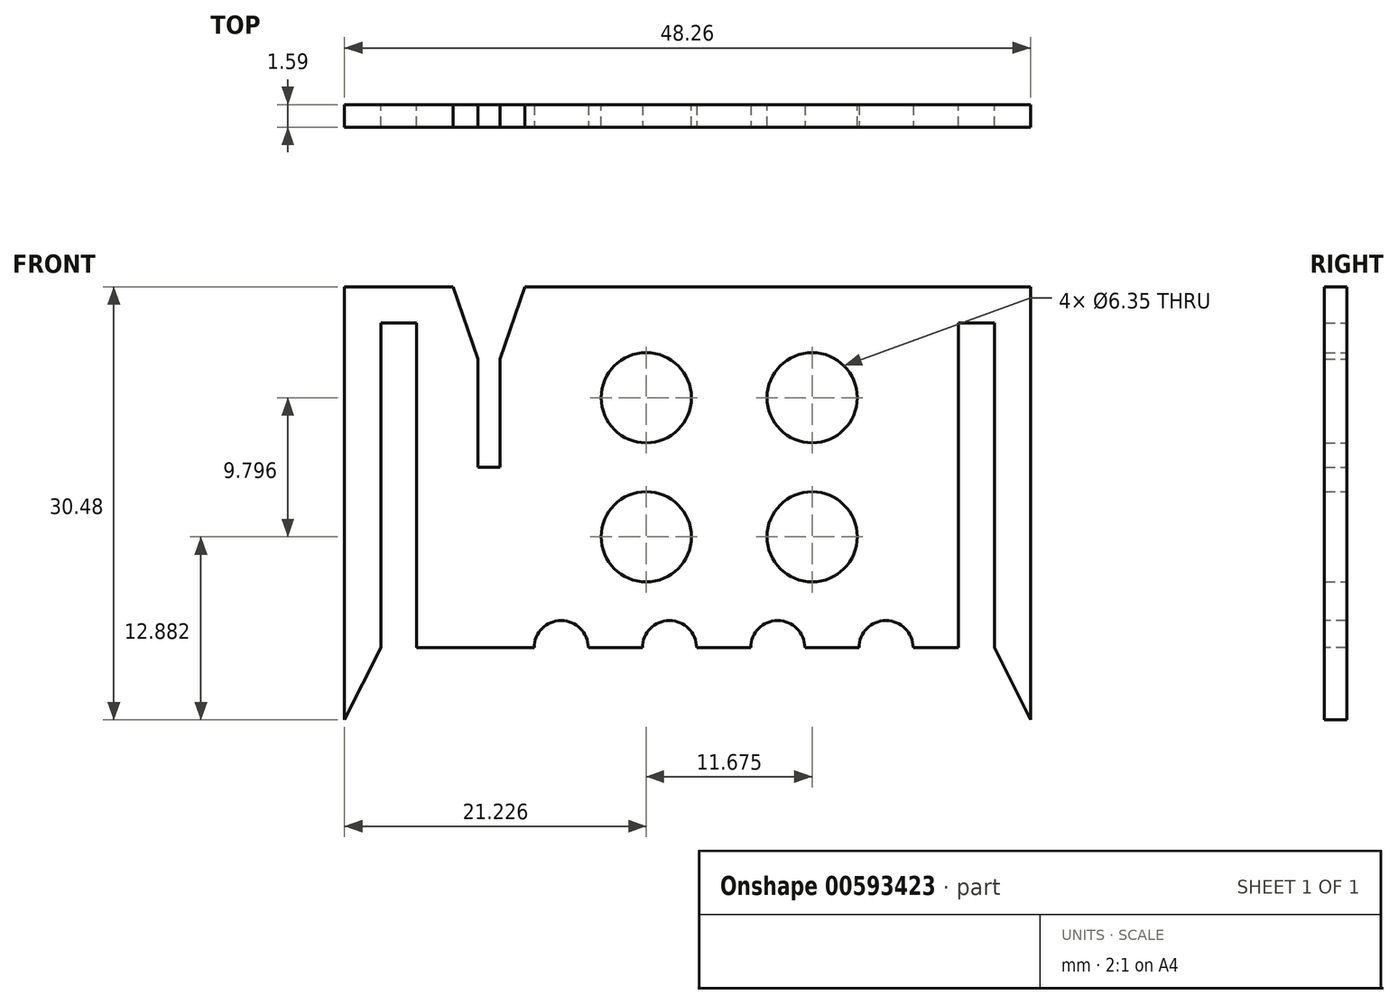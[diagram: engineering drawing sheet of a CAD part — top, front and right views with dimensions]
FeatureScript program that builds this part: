
annotation { "Feature Type Name" : "Feature", "Feature Type Description" : "" }
export const myFeature = defineFeature(function(context is Context, id is Id, definition is map)
    precondition{}
    {
        {
            var Q0;
            Q0=qCreatedBy(makeId("Front.planeOp"),FACE);
            var sketch = newSketch(context, id + "F0", { "sketchPlane" : qUnion([Q0])});
            skLineSegment(sketch, "E0.bottom", {"start": v(0, 0) * mm, "end": v(38.1, 0) * mm});
            skLineSegment(sketch, "E0.top", {"start": v(0, 25.4) * mm, "end": v(38.1, 25.4) * mm});
            skLineSegment(sketch, "E0.left", {"start": v(0, 0) * mm, "end": v(0, 25.4) * mm});
            skLineSegment(sketch, "E0.right", {"start": v(38.1, 0) * mm, "end": v(38.1, 25.4) * mm});
            skSolve(sketch);
        }
        {
            var Q0;
            Q0 = qSketchRegion(id + "F0", true);
            extrude(context, id + "F1", {"entities" : qUnion([Q0]), "depth" : 1.59 * mm, "offsetDistance" : 25.4 * mm});
        }
        {
            var Q0;
            Q0=qCreatedBy(makeId("Front.planeOp"),FACE);
            var sketch = newSketch(context, id + "F2", { "sketchPlane" : qUnion([Q0])});
            skLineSegment(sketch, "E1", {"start": v(38.1, 25.4) * mm, "end": v(43.18, 25.4) * mm});
            skLineSegment(sketch, "E2", {"start": v(43.18, 25.4) * mm, "end": v(43.18, -5.08) * mm});
            skLineSegment(sketch, "E3", {"start": v(43.18, -5.08) * mm, "end": v(40.64, 0) * mm});
            skLineSegment(sketch, "E4", {"start": v(40.64, 0) * mm, "end": v(40.64, 22.86) * mm});
            skLineSegment(sketch, "E5", {"start": v(40.64, 22.86) * mm, "end": v(38.1, 22.86) * mm});
            skLineSegment(sketch, "E6", {"start": v(38.1, 22.86) * mm, "end": v(38.1, 25.4) * mm});
            skLineSegment(sketch, "E7", {"start": v(19.05, 25.4) * mm, "end": v(19.05, 0) * mm, "construction": true});
            skLineSegment(sketch, "E8.MirrorCS", {"start": v(0, 22.86) * mm, "end": v(0, 25.4) * mm});
            skLineSegment(sketch, "E9.MirrorCS", {"start": v(-2.54, 22.86) * mm, "end": v(0, 22.86) * mm});
            skLineSegment(sketch, "E10.MirrorCS", {"start": v(-2.54, 0) * mm, "end": v(-2.54, 22.86) * mm});
            skLineSegment(sketch, "E11.MirrorCS", {"start": v(-5.08, 25.4) * mm, "end": v(-5.08, -5.08) * mm});
            skLineSegment(sketch, "E12.MirrorCS", {"start": v(0, 25.4) * mm, "end": v(-5.08, 25.4) * mm});
            skLineSegment(sketch, "E13.MirrorCS", {"start": v(-5.08, -5.08) * mm, "end": v(-2.54, 0) * mm});
            skSolve(sketch);
        }
        {
            var Q0;
            Q0 = qSketchRegion(id + "F2", true);
            var Q1;
            Q1=makeQuery(id+"F1.opExtrude","CAP_FACE",FACE,{"disambiguationData":[OSD([sQuery(id+"F0.wireOp",EDGE,"E0.bottom"),sQuery(id+"F0.wireOp",EDGE,"E0.top"),sQuery(id+"F0.wireOp",EDGE,"E0.left"),sQuery(id+"F0.wireOp",EDGE,"E0.right")])],"isStart":false});
            extrude(context, id + "F3", {"entities" : qUnion([Q0]), "operationType" : NewBodyOperationType.ADD, "endBound" : BoundingType.UP_TO_SURFACE, "depth" : 25.4 * mm, "endBoundEntityFace" : qUnion([Q1]), "offsetDistance" : 25.4 * mm});
        }
        {
            var Q0;
            Q0=qCreatedBy(makeId("Front.planeOp"),FACE);
            var sketch = newSketch(context, id + "F4", { "sketchPlane" : qUnion([Q0])});
            skLineSegment(sketch, "E14", {"start": v(2.54, 25.4) * mm, "end": v(4.3, 20.32) * mm});
            skLineSegment(sketch, "E15", {"start": v(4.3, 20.32) * mm, "end": v(4.3, 12.7) * mm});
            skLineSegment(sketch, "E16", {"start": v(4.3, 12.7) * mm, "end": v(5.87, 12.7) * mm});
            skLineSegment(sketch, "E17", {"start": v(5.87, 12.7) * mm, "end": v(5.87, 20.32) * mm});
            skLineSegment(sketch, "E18", {"start": v(5.87, 20.32) * mm, "end": v(7.62, 25.4) * mm});
            skLineSegment(sketch, "E19", {"start": v(7.62, 25.4) * mm, "end": v(2.54, 25.4) * mm});
            skLineSegment(sketch, "E20", {"start": v(5.08, 12.7) * mm, "end": v(5.08, 25.4) * mm, "construction": true});
            skSolve(sketch);
        }
        {
            var Q0;
            Q0 = qSketchRegion(id + "F4", true);
            extrude(context, id + "F5", {"entities" : qUnion([Q0]), "operationType" : NewBodyOperationType.REMOVE, "endBound" : BoundingType.THROUGH_ALL, "depth" : 25.4 * mm, "offsetDistance" : 25.4 * mm});
        }
        {
            var Q0;
            Q0=qCreatedBy(makeId("Front.planeOp"),FACE);
            var sketch = newSketch(context, id + "F6", { "sketchPlane" : qUnion([Q0])});
            skCircle(sketch, "E21", {"center": v(16.15, 17.6) * mm, "radius": 3.18 * mm});
            skCircle(sketch, "E22", {"center": v(27.82, 17.6) * mm, "radius": 3.18 * mm});
            skCircle(sketch, "E23", {"center": v(16.15, 7.8) * mm, "radius": 3.18 * mm});
            skCircle(sketch, "E24", {"center": v(27.82, 7.8) * mm, "radius": 3.18 * mm});
            skLineSegment(sketch, "E25", {"start": v(5.87, 16.51) * mm, "end": v(38.1, 16.51) * mm, "construction": true});
            skLineSegment(sketch, "E26", {"start": v(21.98, 16.51) * mm, "end": v(21.98, 0) * mm, "construction": true});
            skLineSegment(sketch, "E27", {"start": v(16.15, 17.6) * mm, "end": v(21.98, 12.7) * mm, "construction": true});
            skLineSegment(sketch, "E28", {"start": v(21.98, 12.7) * mm, "end": v(27.82, 17.6) * mm, "construction": true});
            skLineSegment(sketch, "E29", {"start": v(27.82, 7.8) * mm, "end": v(21.98, 12.7) * mm, "construction": true});
            skLineSegment(sketch, "E30", {"start": v(21.98, 12.7) * mm, "end": v(16.15, 7.8) * mm, "construction": true});
            skLineSegment(sketch, "E31", {"start": v(7.62, 0) * mm, "end": v(7.62, 25.4) * mm, "construction": true});
            skLineSegment(sketch, "E32", {"start": v(7.62, 12.7) * mm, "end": v(38.1, 12.7) * mm, "construction": true});
            skSolve(sketch);
        }
        {
            var Q0;
            Q0 = qSketchRegion(id + "F6", true);
            extrude(context, id + "F7", {"entities" : qUnion([Q0]), "operationType" : NewBodyOperationType.REMOVE, "endBound" : BoundingType.THROUGH_ALL, "depth" : 25.4 * mm, "offsetDistance" : 25.4 * mm});
        }
        {
            var Q0;
            {var subQ0=sQuery(id+"F0.wireOp",EDGE,"E0.right");var subQ1=sQuery(id+"F0.wireOp",EDGE,"E0.left");var subQ2=sQuery(id+"F0.wireOp",EDGE,"E0.top");var subQ3=sQuery(id+"F0.wireOp",EDGE,"E0.bottom");Q0=makeQuery(id+"F3.boolean.opBoolean","MERGE",FACE,{"derivedFrom":[makeQuery(id+"F1.opExtrude","CAP_FACE",FACE,{"disambiguationData":[OSD([subQ3,subQ2,subQ1,subQ0])],"isStart":false}),makeQuery(id+"F3.opExtrude","CAP_FACE",FACE,{"disambiguationData":[OSD([subQ3,subQ2,subQ1,subQ0]),OD(0.0)],"isStart":false}),makeQuery(id+"F3.opExtrude","CAP_FACE",FACE,{"disambiguationData":[OSD([subQ3,subQ2,subQ1,subQ0]),OD(1.0)],"isStart":false})]});}
            var sketch = newSketch(context, id + "F8", { "sketchPlane" : qUnion([Q0])});
            skCircle(sketch, "E33", {"center": v(10.16, 0) * mm, "radius": 1.9 * mm});
            skCircle(sketch, "E34.1.0.0", {"center": v(17.78, 0) * mm, "radius": 1.9 * mm});
            skCircle(sketch, "E34.2.0.0", {"center": v(25.4, 0) * mm, "radius": 1.9 * mm});
            skCircle(sketch, "E34.3.0.0", {"center": v(33.02, 0) * mm, "radius": 1.9 * mm});
            skLineSegment(sketch, "E34.direction1", {"start": v(10.16, 0) * mm, "end": v(17.78, 0) * mm, "construction": true});
            skSolve(sketch);
        }
        {
            var Q0;
            Q0 = qSketchRegion(id + "F8", true);
            extrude(context, id + "F9", {"entities" : qUnion([Q0]), "operationType" : NewBodyOperationType.REMOVE, "oppositeDirection" : true, "depth" : 25.4 * mm, "offsetDistance" : 25.4 * mm});
        }
    });
